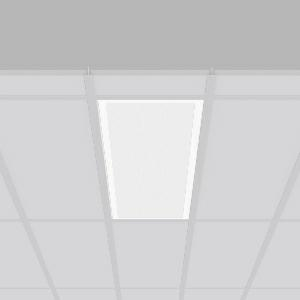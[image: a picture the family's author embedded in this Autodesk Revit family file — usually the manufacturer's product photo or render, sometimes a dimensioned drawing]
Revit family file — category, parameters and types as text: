
# Revit family: sidelite_eco_672373_002_89_ed7c
name_source: partatom
category: Lighting Fixtures
units: mm (PartAtom-declared; Revit-internal decimal feet)

## family parameters
Cut with Voids When Loaded = No
Host = Face
Light Source = No
Part Type = Normal
Room Calculation Point = No
Round Connector Dimension = Use Diameter
Shared = No

## types (1)
- SIDELITE ECO (1 x LED Modul 830, 3150 lm, 3000)
    Apparent Load = 30 VA
    CIE Flux Codes = 60 87 97 100 100
    Color Rendering = 80
    Color Temperature = 3000
    Default Elevation = 1800 mm
    Description = Series: SIDELITE ECO
Highly economical recessed luminaire with progressive LED technology. For escape route illumination. Frame made of aluminium, powder-coated. Diffuser plastic microprismatic. Lightguide and diffuser made of non-yellowing plastic (PMMA). Lateral light emission (RZB SIDELITE technology) for homogeneous light distribution. External driver. Second cable inlet for loop through. With AC Control monitoring module for LUXIFAIR central battery units. External driver with simple plug-in locking system. Extended connection cable (1.90 m). 
Colour: white
Length: 1245 mm
Width: 308 mm
Cut-out length: 1220 mm
Cut-out width: 285 mm
Recess height: 160 mm
Luminaire: recess height: 40 mm
Weight: 4.19 kg
Operating mode: maintained power mode
Lamp: LED
Socket: without socket
Colour temperature: 3000K
Colour rendering index (CRI): 80
System power: 30 W
Rated luminous flux: 3150 lm
Luminous flux, emergency: 3150 lm
System power, emergency: 30 W
Control gear: Regulated power supply
Protection class: I
Type of protection: IP 20
    Height = 0 mm  [stored 0 ft]
    Lamp = 1 x LED Modul 830
    Lamp Light Flux = 3150 lm
    Lamp count = 1
    Length = 1245 mm
    Lifetime = 50000 h
    Luminous efficacy = 105 lm/W
    Manufacturer = RZB
    ModVariant = No
    Model = 672373.002.89
    Mounting Place = Ceiling
    Mounting Type = Recessed
    Number of Poles = 1
    OnlyDefault = Yes
    Power Factor = 1
    Product Name = SIDELITE ECO
    Product group = Recessed modular luminaires
    ProductGroupID = 406
    Protection Class = Protection class I
    Protection Degree = Degree of protection
    RLX_Detail_Level = 1
    RLX_Emergency_Light_Flux = 3150 lm
    RLX_Emergency_Type = 3
    RLX_Emergency_Type_DB = Yes
    RlxData = <blob elided: 34645 chars, md5=6c473108>
    Socket = socket
    Standby Power = 0 W
    System Light Flux = 3150 lm
    System Power = 30 W
    Type Comments = Product without accessories
    Type Image = 312368.002.jpg
    URL = http://relux.com
    VarID = ---
    Voltage = 0 V
    Weight = 0.00 kg
    Width = 308 mm

note: [stored X ft] marks values corroborated as IEEE doubles in the binary element streams (Revit-internal decimal feet)

## geometry (parser evidence)
native form markers: Blend x4, Sweep x12
no freeform markers — native parametric forms only
